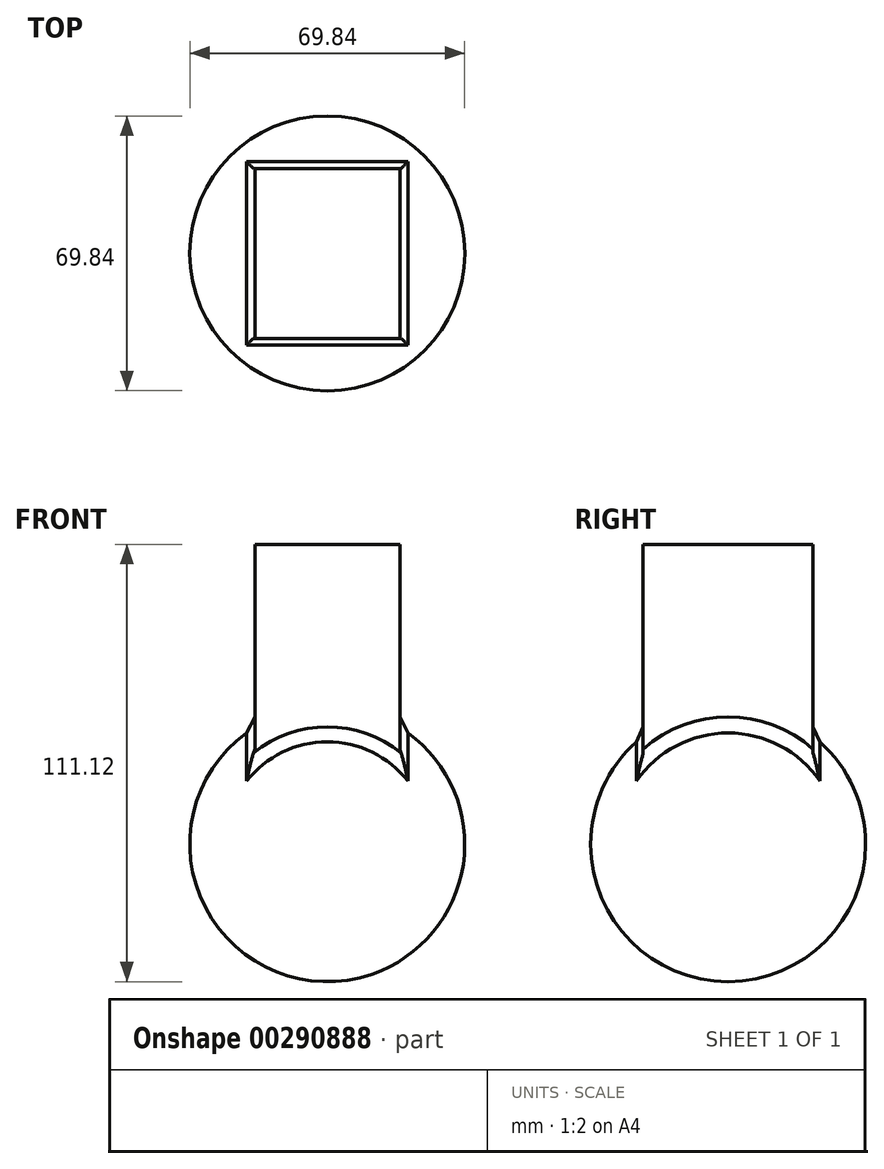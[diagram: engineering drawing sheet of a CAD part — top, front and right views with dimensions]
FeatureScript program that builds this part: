
annotation { "Feature Type Name" : "Feature", "Feature Type Description" : "" }
export const myFeature = defineFeature(function(context is Context, id is Id, definition is map)
    precondition{}
    {
        {
            var Q0;
            Q0=qCreatedBy(makeId("Top.planeOp"),FACE);
            var sketch = newSketch(context, id + "F0", { "sketchPlane" : qUnion([Q0])});
            skArc(sketch, "E0", {"start": v(0, 34.93) * mm, "mid": v(-34.93, 0) * mm, "end": v(0, -34.93) * mm});
            skLineSegment(sketch, "E1", {"start": v(0, 34.93) * mm, "end": v(0, -34.93) * mm});
            skSolve(sketch);
        }
        {
            var Q0;
            Q0=makeQuery(id+"F0.imprint","IMPRINT",FACE,{"disambiguationData":[TD([[makeQuery(id+"F0.imprint","IMPRINT",EDGE,{"derivedFrom":sQuery(id+"F0.wireOp",EDGE,"E0")}),1.0]])]});
            var Q1;
            Q1=sQuery(id+"F0.wireOp",EDGE,"E1");
            revolve(context, id + "F1", {"entities" : qUnion([Q0]), "axis" : qUnion([Q1]), "revolveType" : RevolveType.FULL});
        }
        {
            var Q0;
            Q0=qCreatedBy(makeId("Top.planeOp"),FACE);
            var sketch = newSketch(context, id + "F2", { "sketchPlane" : qUnion([Q0])});
            skLineSegment(sketch, "E2.bottom", {"start": v(-18.41, 21.59) * mm, "end": v(18.42, 21.59) * mm});
            skLineSegment(sketch, "E2.top", {"start": v(-18.42, -21.59) * mm, "end": v(18.41, -21.59) * mm});
            skLineSegment(sketch, "E2.left", {"start": v(-18.41, 21.59) * mm, "end": v(-18.42, -21.59) * mm});
            skLineSegment(sketch, "E2.right", {"start": v(18.42, 21.59) * mm, "end": v(18.41, -21.59) * mm});
            skPoint(sketch, "E2.middle", {"position": v(0, 0) * mm});
            skSolve(sketch);
        }
        {
            var Q0;
            Q0 = qSketchRegion(id + "F2", true);
            extrude(context, id + "F3", {"entities" : qUnion([Q0]), "operationType" : NewBodyOperationType.ADD, "depth" : 76.2 * mm});
        }
        {
            var Q0;
            Q0=makeQuery(id+"F1.opRevolve","SWEPT_FACE",FACE,{"disambiguationData":[OSD([sQuery(id+"F0.wireOp",EDGE,"E0")])]});
            chamfer(context, id + "F4", {"entities" : qUnion([Q0]), "width" : 5.08 * mm, "tangentPropagation" : true});
        }
    });
